# Revit family: Sanitary_Toilets_Toto_CT426CFG-AP-Wall-Hung-Bowl
name_source: partatom
category: Plumbing Fixtures
units: mm (PartAtom-declared; Revit-internal decimal feet)

## family parameters
Cut with Voids When Loaded = No
Host = Face
OmniClass Number = 23.45.05.21.11
OmniClass Title = Water Closets
Part Type = Normal
Room Calculation Point = No
Round Connector Dimension = Use Diameter
Shared = No

## types (1)
- CT428CFG
    Actual Condensate Drain Flow = 0 GPM
    Assembly Code = D2010
    CWFU = 0
    Cold Water Inlet Connection Diameter = 2"
    Default Elevation = 0"
    Depth = 21 1/4"
    Description = AP Wall Hung Bowl
    Edition number = 1
    Height = 16 1/8"
    Keynote = 15410
    Manufacturer = TOTO USA Inc.
    Maximum Pressure (static) = 80.00 psi
    Minimum Water Pressure (flowing) = 8.00 psi
    Model = CT428CFG
    Product Material = Toto - Vitreous China - Cotton
    Sanitary Drain Connection Diameter = 6"
    URL = http://www.totousa.com
    WFU = 0
    Weight = 68.00 lb
    Width = 15"
    Z_Option 1 = Flush : 1.28 GPF
    Z_Option 2 = Flush : 0.9 GPF

## geometry (parser evidence)
native form markers: Sweep x4
no freeform markers — native parametric forms only
